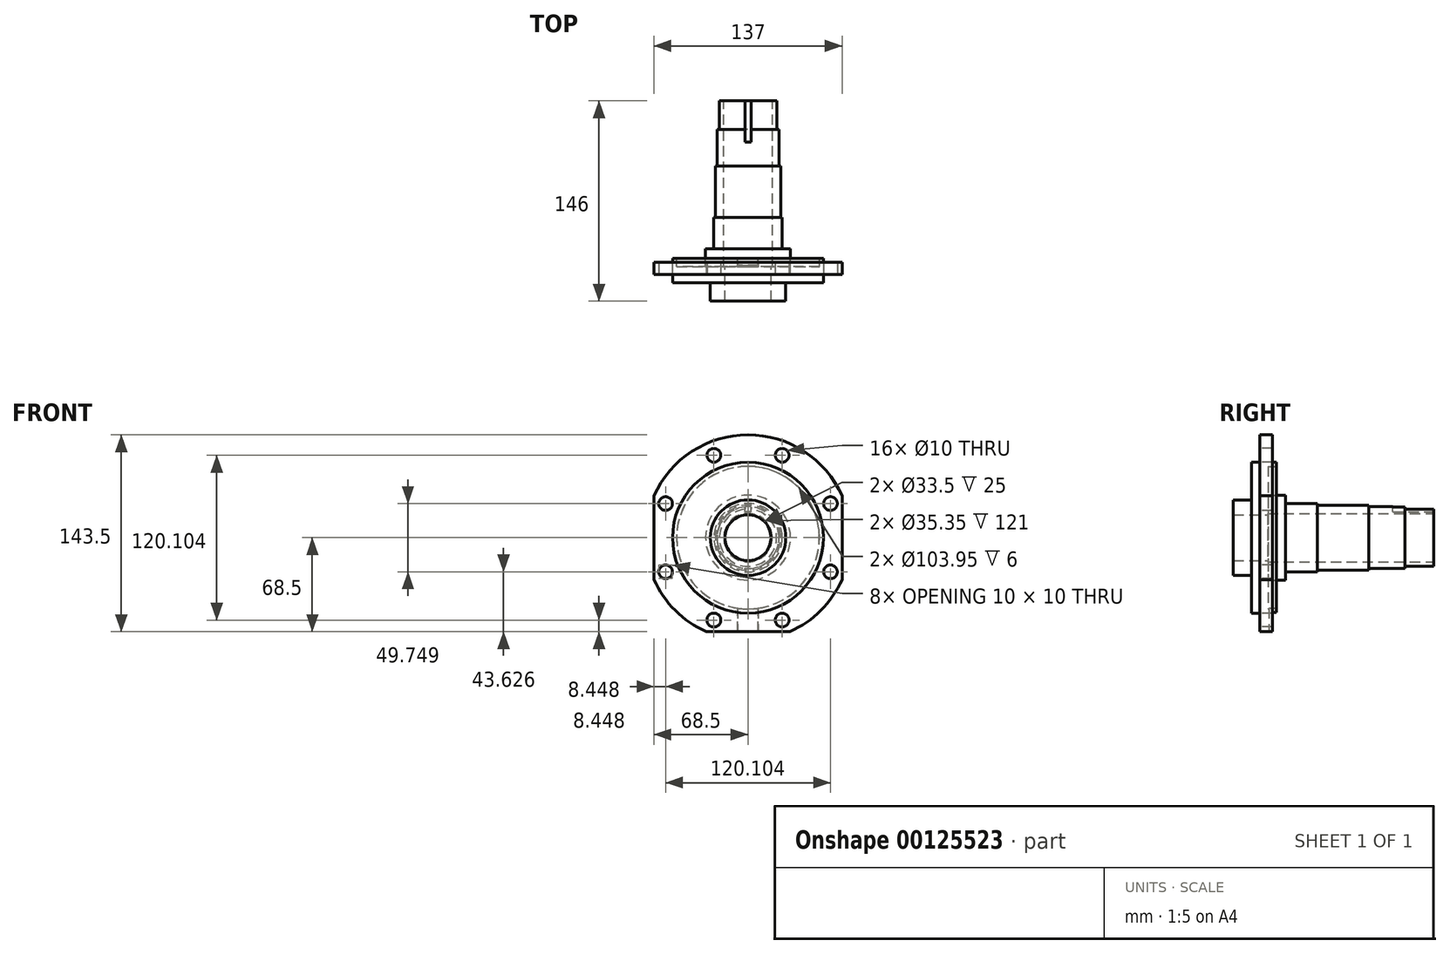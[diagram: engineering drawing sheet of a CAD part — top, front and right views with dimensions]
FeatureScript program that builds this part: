
annotation { "Feature Type Name" : "Feature", "Feature Type Description" : "" }
export const myFeature = defineFeature(function(context is Context, id is Id, definition is map)
    precondition{}
    {
        {
            var Q0;
            Q0=qCreatedBy(makeId("Right.planeOp"),FACE);
            var sketch = newSketch(context, id + "F0", { "sketchPlane" : qUnion([Q0])});
            skLineSegment(sketch, "E0", {"start": v(0, 75) * mm, "end": v(0, 54.98) * mm});
            skLineSegment(sketch, "E1", {"start": v(0, 54.98) * mm, "end": v(3, 54.98) * mm});
            skLineSegment(sketch, "E2", {"start": v(3, 54.98) * mm, "end": v(3, 51.98) * mm});
            skLineSegment(sketch, "E3", {"start": v(3, 51.98) * mm, "end": v(-3, 51.98) * mm});
            skLineSegment(sketch, "E4", {"start": v(-3, 51.98) * mm, "end": v(-3, 30.98) * mm});
            skLineSegment(sketch, "E5", {"start": v(-3, 30.98) * mm, "end": v(9.75, 30.98) * mm});
            skLineSegment(sketch, "E6", {"start": v(9.75, 30.98) * mm, "end": v(9.75, 24.95) * mm});
            skLineSegment(sketch, "E7", {"start": v(9.75, 24.95) * mm, "end": v(32.75, 24.95) * mm});
            skLineSegment(sketch, "E8", {"start": v(32.75, 24.95) * mm, "end": v(32.75, 23.72) * mm});
            skLineSegment(sketch, "E9", {"start": v(32.75, 23.72) * mm, "end": v(70.25, 23.73) * mm});
            skLineSegment(sketch, "E10", {"start": v(70.25, 23.73) * mm, "end": v(70.25, 22.57) * mm});
            skLineSegment(sketch, "E11", {"start": v(70.25, 22.57) * mm, "end": v(96.75, 22.58) * mm});
            skLineSegment(sketch, "E12", {"start": v(96.75, 22.58) * mm, "end": v(96.75, 20.87) * mm});
            skLineSegment(sketch, "E13", {"start": v(96.75, 20.87) * mm, "end": v(117.75, 20.88) * mm});
            skLineSegment(sketch, "E14", {"start": v(117.75, 20.88) * mm, "end": v(117.75, 17.68) * mm});
            skLineSegment(sketch, "E15", {"start": v(117.75, 17.68) * mm, "end": v(-3.25, 17.67) * mm});
            skLineSegment(sketch, "E16", {"start": v(-3.25, 17.67) * mm, "end": v(-3.25, 16.75) * mm});
            skLineSegment(sketch, "E17", {"start": v(-3.25, 16.75) * mm, "end": v(-28.25, 16.75) * mm});
            skLineSegment(sketch, "E18", {"start": v(-28.25, 16.75) * mm, "end": v(-28.25, 27.5) * mm});
            skLineSegment(sketch, "E19", {"start": v(-28.25, 27.5) * mm, "end": v(-15, 27.5) * mm});
            skLineSegment(sketch, "E20", {"start": v(-15, 27.5) * mm, "end": v(-15, 54.98) * mm});
            skLineSegment(sketch, "E21", {"start": v(-15, 54.98) * mm, "end": v(-9, 54.98) * mm});
            skLineSegment(sketch, "E22", {"start": v(-9, 54.98) * mm, "end": v(-9, 75) * mm});
            skLineSegment(sketch, "E23", {"start": v(-9, 75) * mm, "end": v(0, 75) * mm});
            skLineSegment(sketch, "E24.MirrorCS", {"start": v(-3.25, -17.67) * mm, "end": v(-3.25, -16.75) * mm});
            skLineSegment(sketch, "E25.MirrorCS", {"start": v(9.75, -30.98) * mm, "end": v(9.75, -24.95) * mm});
            skLineSegment(sketch, "E26.MirrorCS", {"start": v(70.25, -23.73) * mm, "end": v(70.25, -22.57) * mm});
            skLineSegment(sketch, "E27.MirrorCS", {"start": v(0, -54.98) * mm, "end": v(3, -54.98) * mm});
            skLineSegment(sketch, "E28.MirrorCS", {"start": v(3, -54.98) * mm, "end": v(3, -51.98) * mm});
            skLineSegment(sketch, "E29.MirrorCS", {"start": v(96.75, -22.58) * mm, "end": v(96.75, -20.87) * mm});
            skLineSegment(sketch, "E30.MirrorCS", {"start": v(117.75, -20.88) * mm, "end": v(117.75, -17.68) * mm});
            skLineSegment(sketch, "E31.MirrorCS", {"start": v(-3, -30.98) * mm, "end": v(9.75, -30.98) * mm});
            skLineSegment(sketch, "E32.MirrorCS", {"start": v(-3, -51.98) * mm, "end": v(-3, -30.98) * mm});
            skLineSegment(sketch, "E33.MirrorCS", {"start": v(-28.25, -16.75) * mm, "end": v(-28.25, -27.5) * mm});
            skLineSegment(sketch, "E34.MirrorCS", {"start": v(9.75, -24.95) * mm, "end": v(32.75, -24.95) * mm});
            skLineSegment(sketch, "E35.MirrorCS", {"start": v(32.75, -24.95) * mm, "end": v(32.75, -23.72) * mm});
            skLineSegment(sketch, "E36.MirrorCS", {"start": v(3, -51.98) * mm, "end": v(-3, -51.98) * mm});
            skLineSegment(sketch, "E37.MirrorCS", {"start": v(32.75, -23.72) * mm, "end": v(70.25, -23.73) * mm});
            skLineSegment(sketch, "E38.MirrorCS", {"start": v(-15, -27.5) * mm, "end": v(-15, -54.98) * mm});
            skLineSegment(sketch, "E39.MirrorCS", {"start": v(70.25, -22.57) * mm, "end": v(96.75, -22.58) * mm});
            skLineSegment(sketch, "E40.MirrorCS", {"start": v(0, -75) * mm, "end": v(0, -54.98) * mm});
            skLineSegment(sketch, "E41.MirrorCS", {"start": v(-9, -54.98) * mm, "end": v(-9, -75) * mm});
            skLineSegment(sketch, "E42.MirrorCS", {"start": v(-15, -54.98) * mm, "end": v(-9, -54.98) * mm});
            skLineSegment(sketch, "E43.MirrorCS", {"start": v(117.75, -17.68) * mm, "end": v(-3.25, -17.67) * mm});
            skLineSegment(sketch, "E44.MirrorCS", {"start": v(-28.25, -27.5) * mm, "end": v(-15, -27.5) * mm});
            skLineSegment(sketch, "E45.MirrorCS", {"start": v(-9, -75) * mm, "end": v(0, -75) * mm});
            skLineSegment(sketch, "E46.MirrorCS", {"start": v(-3.25, -16.75) * mm, "end": v(-28.25, -16.75) * mm});
            skLineSegment(sketch, "E47.MirrorCS", {"start": v(96.75, -20.87) * mm, "end": v(117.75, -20.88) * mm});
            skLineSegment(sketch, "E48", {"start": v(0, 0) * mm, "end": v(-31.8, 0) * mm});
            skSolve(sketch);
        }
        {
            var Q0;
            Q0 = qSketchRegion(id + "F0", true);
            var Q1;
            Q1=sQuery(id+"F0.wireOp",EDGE,"E48");
            revolve(context, id + "F1", {"entities" : qUnion([Q0]), "axis" : qUnion([Q1]), "revolveType" : RevolveType.FULL});
        }
        {
            var Q0;
            Q0=qCreatedBy(makeId("Front.planeOp"),FACE);
            var sketch = newSketch(context, id + "F2", { "sketchPlane" : qUnion([Q0])});
            skLineSegment(sketch, "E49", {"start": v(68.5, 30.54) * mm, "end": v(68.5, -30.54) * mm});
            skLineSegment(sketch, "E50", {"start": v(68.5, 30.54) * mm, "end": v(80.56, 30.54) * mm});
            skLineSegment(sketch, "E51", {"start": v(80.56, 30.54) * mm, "end": v(80.56, -30.54) * mm});
            skLineSegment(sketch, "E52", {"start": v(80.56, -30.54) * mm, "end": v(68.5, -30.54) * mm});
            skLineSegment(sketch, "E53", {"start": v(0, 0) * mm, "end": v(24.87, 60.05) * mm, "construction": true});
            skLineSegment(sketch, "E54", {"start": v(0, 0) * mm, "end": v(0, 73.64) * mm, "construction": true});
            skCircle(sketch, "E55", {"center": v(24.87, 60.05) * mm, "radius": 5 * mm});
            skCircle(sketch, "E56.1.0", {"center": v(60.05, 24.87) * mm, "radius": 5 * mm});
            skCircle(sketch, "E56.2.0", {"center": v(60.05, -24.87) * mm, "radius": 5 * mm});
            skCircle(sketch, "E56.3.0", {"center": v(24.87, -60.05) * mm, "radius": 5 * mm});
            skCircle(sketch, "E56.4.0", {"center": v(-24.87, -60.05) * mm, "radius": 5 * mm});
            skCircle(sketch, "E56.5.0", {"center": v(-60.05, -24.87) * mm, "radius": 5 * mm});
            skCircle(sketch, "E56.6.0", {"center": v(-60.05, 24.87) * mm, "radius": 5 * mm});
            skCircle(sketch, "E56.7.0", {"center": v(-24.87, 60.05) * mm, "radius": 5 * mm});
            skPoint(sketch, "E56.center", {"position": v(0, 0) * mm});
            skLineSegment(sketch, "E56.anchor2", {"start": v(0, 0) * mm, "end": v(-24.87, 60.05) * mm, "construction": true});
            skLineSegment(sketch, "E57.1.0", {"start": v(30.54, -68.5) * mm, "end": v(-30.54, -68.5) * mm});
            skLineSegment(sketch, "E57.1.1", {"start": v(30.54, -68.5) * mm, "end": v(30.54, -80.56) * mm});
            skLineSegment(sketch, "E57.1.2", {"start": v(30.54, -80.56) * mm, "end": v(-30.54, -80.56) * mm});
            skLineSegment(sketch, "E57.1.3", {"start": v(-30.54, -80.56) * mm, "end": v(-30.54, -68.5) * mm});
            skLineSegment(sketch, "E57.2.0", {"start": v(-68.5, -30.54) * mm, "end": v(-68.5, 30.54) * mm});
            skLineSegment(sketch, "E57.2.1", {"start": v(-68.5, -30.54) * mm, "end": v(-80.56, -30.54) * mm});
            skLineSegment(sketch, "E57.2.2", {"start": v(-80.56, -30.54) * mm, "end": v(-80.56, 30.54) * mm});
            skLineSegment(sketch, "E57.2.3", {"start": v(-80.56, 30.54) * mm, "end": v(-68.5, 30.54) * mm});
            skLineSegment(sketch, "E57.anchor1", {"start": v(0, 0) * mm, "end": v(68.5, -30.54) * mm, "construction": true});
            skLineSegment(sketch, "E57.anchor2", {"start": v(0, 0) * mm, "end": v(-68.5, 30.54) * mm, "construction": true});
            skSolve(sketch);
        }
        {
            var Q0;
            Q0 = qSketchRegion(id + "F2", true);
            extrude(context, id + "F3", {"entities" : qUnion([Q0]), "operationType" : NewBodyOperationType.REMOVE, "endBound" : BoundingType.THROUGH_ALL, "oppositeDirection" : true, "depth" : 25 * mm, "hasSecondDirection" : true, "secondDirectionBound" : BoundingType.THROUGH_ALL, "secondDirectionOppositeDirection" : false, "secondDirectionDepth" : 25 * mm});
        }
        {
            var Q0;
            Q0=makeQuery(id+"F1.opRevolve","SWEPT_FACE",FACE,{"disambiguationData":[OSD([sQuery(id+"F0.wireOp",EDGE,"E14")])]});
            var sketch = newSketch(context, id + "F4", { "sketchPlane" : qUnion([Q0])});
            skLineSegment(sketch, "E58.bottom", {"start": v(0, 18.93) * mm, "end": v(2.25, 18.93) * mm});
            skLineSegment(sketch, "E58.top", {"start": v(0, 22.93) * mm, "end": v(2.25, 22.93) * mm});
            skLineSegment(sketch, "E58.left", {"start": v(0, 18.93) * mm, "end": v(0, 22.93) * mm});
            skLineSegment(sketch, "E58.right", {"start": v(2.25, 18.93) * mm, "end": v(2.25, 22.93) * mm});
            skLineSegment(sketch, "E59.bottom", {"start": v(0, 18.93) * mm, "end": v(-2.25, 18.93) * mm});
            skLineSegment(sketch, "E59.top", {"start": v(0, 22.93) * mm, "end": v(-2.25, 22.93) * mm});
            skLineSegment(sketch, "E59.left", {"start": v(0, 18.93) * mm, "end": v(0, 22.93) * mm, "construction": true});
            skLineSegment(sketch, "E59.right", {"start": v(-2.25, 18.93) * mm, "end": v(-2.25, 22.93) * mm});
            skSolve(sketch);
        }
        {
            var Q0;
            Q0 = qSketchRegion(id + "F4", true);
            extrude(context, id + "F5", {"entities" : qUnion([Q0]), "operationType" : NewBodyOperationType.REMOVE, "oppositeDirection" : true, "depth" : 30 * mm});
        }
        {
            var Q0;
            Q0=makeQuery(id+"F3.boolean.opBoolean","COPY",FACE,{"disambiguationData":[OD(0.0)],"derivedFrom":makeQuery(id+"F3.opExtrude","SWEPT_FACE",FACE,{"disambiguationData":[OSD([sQuery(id+"F2.wireOp",EDGE,"E57.1.0")])]})});
            var sketch = newSketch(context, id + "F6", { "sketchPlane" : qUnion([Q0])});
            skLineSegment(sketch, "E60.bottom", {"start": v(7.5, -5.75) * mm, "end": v(-7.5, -5.75) * mm});
            skLineSegment(sketch, "E60.top", {"start": v(7.5, 2.25) * mm, "end": v(-7.5, 2.25) * mm});
            skLineSegment(sketch, "E60.left", {"start": v(7.5, -5.75) * mm, "end": v(7.5, 2.25) * mm});
            skLineSegment(sketch, "E60.right", {"start": v(-7.5, -5.75) * mm, "end": v(-7.5, 2.25) * mm});
            skLineSegment(sketch, "E61", {"start": v(0, 2.25) * mm, "end": v(0, 0) * mm});
            skLineSegment(sketch, "E62", {"start": v(0, 0) * mm, "end": v(0, -5.75) * mm});
            skLineSegment(sketch, "E63", {"start": v(7.5, 0) * mm, "end": v(0, 0) * mm});
            skSolve(sketch);
        }
        {
            var Q0;
            Q0 = qSketchRegion(id + "F6", true);
            var Q1;
            Q1=makeQuery(id+"F1.opRevolve","SWEPT_FACE",FACE,{"disambiguationData":[OSD([sQuery(id+"F0.wireOp",EDGE,"E5")])]});
            extrude(context, id + "F7", {"entities" : qUnion([Q0]), "operationType" : NewBodyOperationType.REMOVE, "endBound" : BoundingType.UP_TO_SURFACE, "oppositeDirection" : true, "endBoundEntityFace" : qUnion([Q1]), "depth" : 25 * mm});
        }
    });
